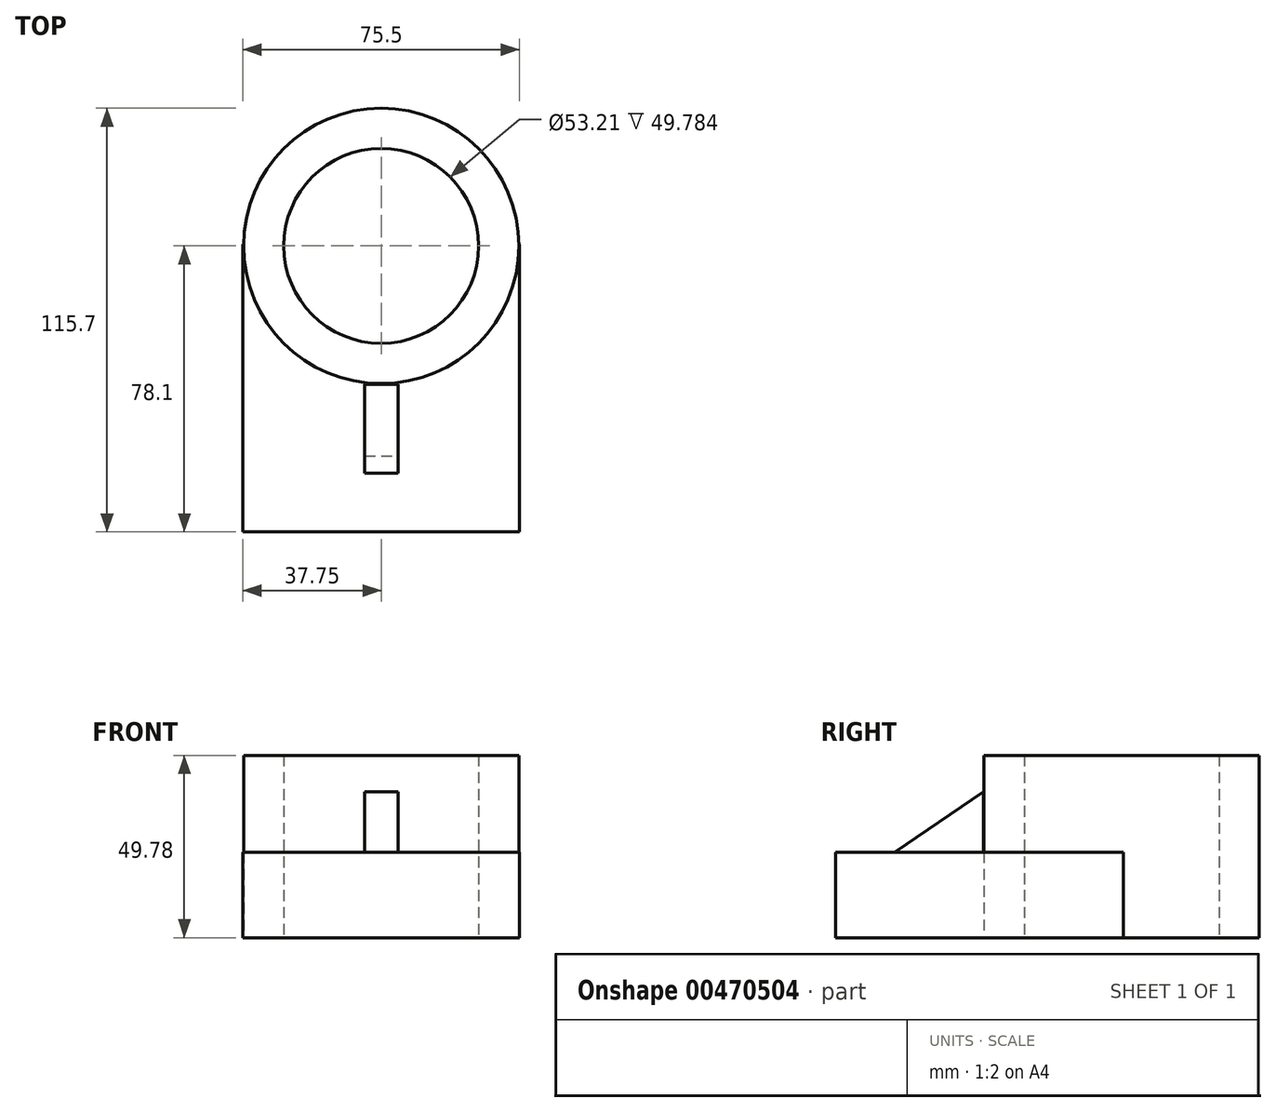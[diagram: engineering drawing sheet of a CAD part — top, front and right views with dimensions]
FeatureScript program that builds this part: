
annotation { "Feature Type Name" : "Feature", "Feature Type Description" : "" }
export const myFeature = defineFeature(function(context is Context, id is Id, definition is map)
    precondition{}
    {
        {
            var Q0;
            Q0=qCreatedBy(makeId("Top.planeOp"),FACE);
            var sketch = newSketch(context, id + "F0", { "sketchPlane" : qUnion([Q0])});
            skCircle(sketch, "E0", {"center": v(0, 38.85) * mm, "radius": 37.6 * mm});
            skLineSegment(sketch, "E1.bottom", {"start": v(37.75, -39.25) * mm, "end": v(-37.75, -39.25) * mm});
            skLineSegment(sketch, "E1.top", {"start": v(37.75, 39.25) * mm, "end": v(37.6, 39.25) * mm});
            skLineSegment(sketch, "E1.left", {"start": v(37.75, -39.25) * mm, "end": v(37.75, 39.25) * mm});
            skLineSegment(sketch, "E1.right", {"start": v(-37.75, -39.25) * mm, "end": v(-37.75, 39.25) * mm});
            skPoint(sketch, "E1.middle", {"position": v(0, 0) * mm});
            skLineSegment(sketch, "E2.trimOffspring", {"start": v(-37.6, 39.25) * mm, "end": v(-37.75, 39.25) * mm});
            skCircle(sketch, "E3", {"center": v(0, 38.85) * mm, "radius": 26.6 * mm});
            skSolve(sketch);
        }
        {
            var Q0;
            {var subQ0=sQuery(id+"F0.wireOp",EDGE,"E0");var subQ1=makeQuery(id+"F0.imprint","INTERSECT",VERTEX,{"derivedFrom":[subQ0,sQuery(id+"F0.wireOp",EDGE,"E1.top")]});Q0=makeQuery(id+"F0.imprint","IMPRINT",FACE,{"disambiguationData":[TD([[makeQuery(id+"F0.imprint","IMPRINT",EDGE,{"disambiguationData":[TD([[subQ1,-1.0]])],"derivedFrom":subQ0}),1.0]])]});}
            extrude(context, id + "F1", {"entities" : qUnion([Q0]), "depth" : 49.78 * mm});
        }
        {
            var Q0;
            Q0=makeQuery(id+"F0.imprint","IMPRINT",FACE,{"disambiguationData":[TD([[makeQuery(id+"F0.imprint","IMPRINT",EDGE,{"derivedFrom":sQuery(id+"F0.wireOp",EDGE,"E1.bottom")}),-1.0]])]});
            var Q1;
            Q1=makeQuery(id+"F0.imprint","IMPRINT",FACE,{"disambiguationData":[TD([[makeQuery(id+"F0.imprint","IMPRINT",EDGE,{"derivedFrom":sQuery(id+"F0.wireOp",EDGE,"4Nus5lI9-D3sP-HiSb-hbkE-gQl6QoK1TUkF")}),1.0]])]});
            var Q2;
            Q2=makeQuery(id+"F0.imprint","IMPRINT",FACE,{"disambiguationData":[TD([[makeQuery(id+"F0.imprint","IMPRINT",EDGE,{"derivedFrom":sQuery(id+"F0.wireOp",EDGE,"4Nus5lI9-D3sP-HiSb-hbkE-gQl6QoK1TUkF")}),-1.0]])]});
            extrude(context, id + "F2", {"entities" : qUnion([Q0, Q1, Q2]), "depth" : 23.37 * mm});
        }
        {
            var Q0;
            Q0=qCreatedBy(makeId("Right.planeOp"),FACE);
            var sketch = newSketch(context, id + "F3", { "sketchPlane" : qUnion([Q0])});
            skLineSegment(sketch, "E4", {"start": v(1.1, 23.46) * mm, "end": v(1.1, 39.85) * mm});
            skLineSegment(sketch, "E5", {"start": v(1.1, 39.85) * mm, "end": v(-23.2, 23.35) * mm});
            skLineSegment(sketch, "E6", {"start": v(-23.2, 23.35) * mm, "end": v(1.1, 23.46) * mm});
            skSolve(sketch);
        }
        {
            var Q0;
            Q0 = qSketchRegion(id + "F3", true);
            extrude(context, id + "F4", {"entities" : qUnion([Q0]), "operationType" : NewBodyOperationType.ADD, "endBound" : BoundingType.SYMMETRIC, "depth" : 9.14 * mm});
        }
    });
